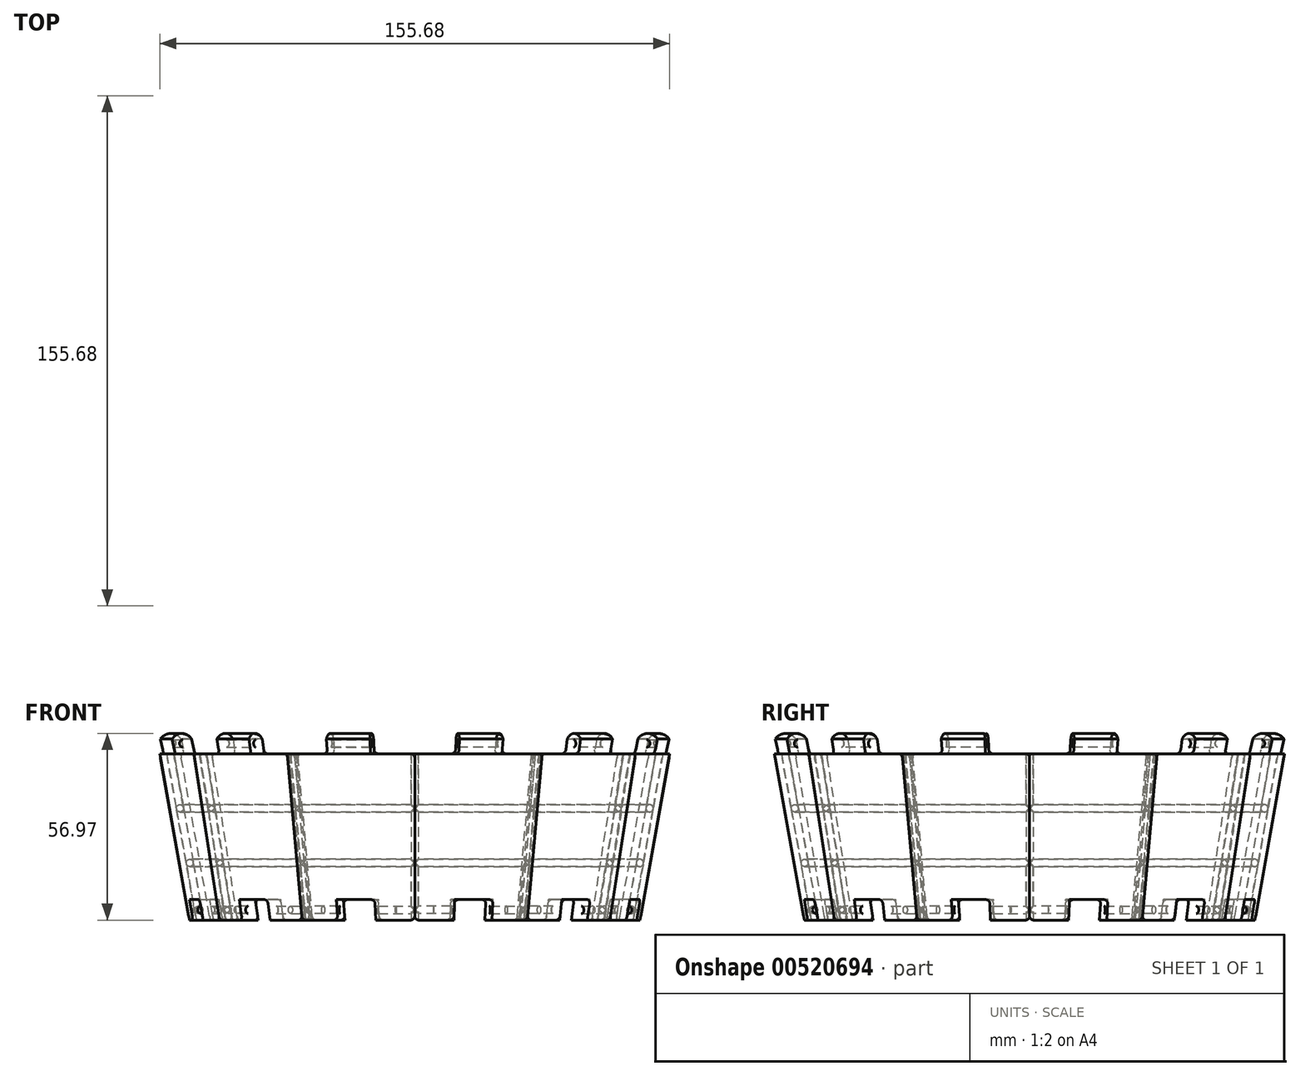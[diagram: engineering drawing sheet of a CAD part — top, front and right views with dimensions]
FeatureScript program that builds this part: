
annotation { "Feature Type Name" : "Feature", "Feature Type Description" : "" }
export const myFeature = defineFeature(function(context is Context, id is Id, definition is map)
    precondition{}
    {
        {
            var Q0;
            Q0=qCreatedBy(makeId("Front.planeOp"),FACE);
            var sketch = newSketch(context, id + "F0", { "sketchPlane" : qUnion([Q0])});
            skLineSegment(sketch, "E0", {"start": v(0, 0) * mm, "end": v(0, 50.8) * mm});
            skLineSegment(sketch, "E1", {"start": v(0, 50.8) * mm, "end": v(77.84, 50.8) * mm});
            skLineSegment(sketch, "E2", {"start": v(0, 0) * mm, "end": v(68.76, 0) * mm});
            skLineSegment(sketch, "E3", {"start": v(68.76, 0) * mm, "end": v(77.84, 50.8) * mm});
            skSolve(sketch);
        }
        {
            var Q0;
            Q0 = qSketchRegion(id + "F0", true);
            var Q1;
            Q1=sQuery(id+"F0.wireOp",EDGE,"E0");
            revolve(context, id + "F1", {"entities" : qUnion([Q0]), "axis" : qUnion([Q1]), "revolveType" : RevolveType.ONE_DIRECTION, "angle" : 30 * degree});
        }
        {
            var Q0;
            Q0=makeQuery(id+"F1.opRevolve","CAP_FACE",FACE,{"disambiguationData":[OSD([sQuery(id+"F0.wireOp",EDGE,"E0"),sQuery(id+"F0.wireOp",EDGE,"E1"),sQuery(id+"F0.wireOp",EDGE,"E2"),sQuery(id+"F0.wireOp",EDGE,"E3")])],"isStart":true});
            var sketch = newSketch(context, id + "F2", { "sketchPlane" : qUnion([Q0])});
            skLineSegment(sketch, "E4", {"start": v(0, 0) * mm, "end": v(0, 50.8) * mm});
            skLineSegment(sketch, "E5", {"start": v(0, 50.8) * mm, "end": v(71.49, 50.8) * mm});
            skLineSegment(sketch, "E6", {"start": v(0, 0) * mm, "end": v(62.4, 0) * mm});
            skLineSegment(sketch, "E7", {"start": v(62.4, 0) * mm, "end": v(71.49, 50.8) * mm});
            skSolve(sketch);
        }
        {
            var Q0;
            Q0 = qSketchRegion(id + "F2", true);
            var Q1;
            Q1=sQuery(id+"F2.wireOp",EDGE,"E4");
            revolve(context, id + "F3", {"operationType" : NewBodyOperationType.REMOVE, "entities" : qUnion([Q0]), "axis" : qUnion([Q1]), "revolveType" : RevolveType.FULL, "oppositeDirection" : true});
        }
        {
            var Q0;
            Q0=makeQuery(id+"F1.opRevolve","CAP_FACE",FACE,{"disambiguationData":[OSD([sQuery(id+"F0.wireOp",EDGE,"E0"),sQuery(id+"F0.wireOp",EDGE,"E1"),sQuery(id+"F0.wireOp",EDGE,"E2"),sQuery(id+"F0.wireOp",EDGE,"E3")])],"isStart":true});
            var sketch = newSketch(context, id + "F4", { "sketchPlane" : qUnion([Q0])});
            skLineSegment(sketch, "E8", {"start": v(0, 0) * mm, "end": v(0, 50.8) * mm, "construction": true});
            skLineSegment(sketch, "E9", {"start": v(0, 0) * mm, "end": v(68.76, 0) * mm, "construction": true});
            skLineSegment(sketch, "E10", {"start": v(68.76, 0) * mm, "end": v(69.88, 6.25) * mm});
            skLineSegment(sketch, "E11", {"start": v(69.88, 6.25) * mm, "end": v(63.53, 6.25) * mm});
            skLineSegment(sketch, "E12", {"start": v(63.53, 6.25) * mm, "end": v(62.4, 0) * mm});
            skLineSegment(sketch, "E13", {"start": v(68.76, 0) * mm, "end": v(62.4, 0) * mm});
            skSolve(sketch);
        }
        {
            var Q0;
            Q0 = qSketchRegion(id + "F4", true);
            var Q1;
            Q1=sQuery(id+"F4.wireOp",EDGE,"E8");
            revolve(context, id + "F5", {"operationType" : NewBodyOperationType.REMOVE, "entities" : qUnion([Q0]), "axis" : qUnion([Q1]), "revolveType" : RevolveType.ONE_DIRECTION, "angle" : 20 * degree});
        }
        {
            var Q0;
            Q0 = qSketchRegion(id + "F4", true);
            var Q1;
            Q1=sQuery(id+"F4.wireOp",EDGE,"E8");
            revolve(context, id + "F6", {"operationType" : NewBodyOperationType.ADD, "entities" : qUnion([Q0]), "axis" : qUnion([Q1]), "revolveType" : RevolveType.ONE_DIRECTION, "angle" : 10 * degree});
        }
        {
            var Q0;
            Q0=makeQuery(id+"F6.boolean.opBoolean","MERGE",FACE,{"derivedFrom":[makeQuery(id+"F1.opRevolve","CAP_FACE",FACE,{"disambiguationData":[OSD([sQuery(id+"F0.wireOp",EDGE,"E0"),sQuery(id+"F0.wireOp",EDGE,"E1"),sQuery(id+"F0.wireOp",EDGE,"E2"),sQuery(id+"F0.wireOp",EDGE,"E3")])],"isStart":true}),makeQuery(id+"F6.opRevolve","CAP_FACE",FACE,{"disambiguationData":[OSD([sQuery(id+"F4.wireOp",EDGE,"E10"),sQuery(id+"F4.wireOp",EDGE,"E11"),sQuery(id+"F4.wireOp",EDGE,"E12"),sQuery(id+"F4.wireOp",EDGE,"E13")])],"isStart":true})]});
            var sketch = newSketch(context, id + "F7", { "sketchPlane" : qUnion([Q0])});
            skLineSegment(sketch, "E14", {"start": v(0, 0) * mm, "end": v(0, 50.8) * mm, "construction": true});
            skLineSegment(sketch, "E15", {"start": v(77.84, 50.8) * mm, "end": v(68.76, 0) * mm, "construction": true});
            skLineSegment(sketch, "E16", {"start": v(77.84, 50.8) * mm, "end": v(71.49, 50.8) * mm});
            skLineSegment(sketch, "E17", {"start": v(0, 50.8) * mm, "end": v(0, 101.6) * mm, "construction": true});
            skLineSegment(sketch, "E18", {"start": v(0, 101.6) * mm, "end": v(88.9, 101.6) * mm, "construction": true});
            skLineSegment(sketch, "E19", {"start": v(88.9, 101.6) * mm, "end": v(77.84, 50.8) * mm, "construction": true});
            skLineSegment(sketch, "E20", {"start": v(77.84, 50.8) * mm, "end": v(79.19, 57) * mm});
            skLineSegment(sketch, "E21", {"start": v(79.19, 57) * mm, "end": v(72.84, 57) * mm});
            skLineSegment(sketch, "E22", {"start": v(72.84, 57) * mm, "end": v(71.49, 50.8) * mm});
            skSolve(sketch);
        }
        {
            var Q0;
            Q0 = qSketchRegion(id + "F7", true);
            var Q1;
            Q1=sQuery(id+"F7.wireOp",EDGE,"E14");
            revolve(context, id + "F8", {"operationType" : NewBodyOperationType.ADD, "entities" : qUnion([Q0]), "axis" : qUnion([Q1]), "revolveType" : RevolveType.ONE_DIRECTION, "angle" : 20 * degree});
        }
        {
            var Q0;
            Q0 = qSketchRegion(id + "F7", true);
            var Q1;
            Q1=sQuery(id+"F7.wireOp",EDGE,"E14");
            revolve(context, id + "F9", {"operationType" : NewBodyOperationType.REMOVE, "entities" : qUnion([Q0]), "axis" : qUnion([Q1]), "revolveType" : RevolveType.ONE_DIRECTION, "angle" : 10 * degree});
        }
        {
            var Q0;
            Q0=makeQuery(id+"F5.boolean.opBoolean","COPY",EDGE,{"derivedFrom":makeQuery(id+"F5.opRevolve","CAP_EDGE",EDGE,{"disambiguationData":[OSD([sQuery(id+"F4.wireOp",EDGE,"E11")])],"isStart":false})});
            var Q1;
            Q1=makeQuery(id+"F6.opRevolve","CAP_EDGE",EDGE,{"disambiguationData":[OSD([sQuery(id+"F4.wireOp",EDGE,"E11")])],"isStart":false});
            var Q2;
            Q2=makeQuery(id+"F6.opRevolve","CAP_EDGE",EDGE,{"disambiguationData":[OSD([sQuery(id+"F4.wireOp",EDGE,"E13")])],"isStart":false});
            var Q3;
            Q3=makeQuery(id+"F5.boolean.opBoolean","COPY",EDGE,{"derivedFrom":makeQuery(id+"F5.opRevolve","CAP_EDGE",EDGE,{"disambiguationData":[OSD([sQuery(id+"F4.wireOp",EDGE,"E13")])],"isStart":false})});
            var Q4;
            Q4=makeQuery(id+"F6.opRevolve","CAP_EDGE",EDGE,{"disambiguationData":[OSD([sQuery(id+"F4.wireOp",EDGE,"E13")])],"isStart":true});
            var Q5;
            Q5=makeQuery(id+"F1.opRevolve","CAP_EDGE",EDGE,{"disambiguationData":[OSD([sQuery(id+"F0.wireOp",EDGE,"E2")])],"isStart":false});
            var Q6;
            Q6=makeQuery(id+"F8.opRevolve","CAP_EDGE",EDGE,{"disambiguationData":[OSD([sQuery(id+"F7.wireOp",EDGE,"E16")])],"isStart":false});
            var Q7;
            Q7=makeQuery(id+"F1.opRevolve","CAP_EDGE",EDGE,{"disambiguationData":[OSD([sQuery(id+"F0.wireOp",EDGE,"E1")])],"isStart":false});
            var Q8;
            Q8=makeQuery(id+"F8.opRevolve","CAP_EDGE",EDGE,{"disambiguationData":[OSD([sQuery(id+"F7.wireOp",EDGE,"E21")])],"isStart":false});
            var Q9;
            Q9=makeQuery(id+"F9.boolean.opBoolean","COPY",EDGE,{"derivedFrom":makeQuery(id+"F9.opRevolve","CAP_EDGE",EDGE,{"disambiguationData":[OSD([sQuery(id+"F7.wireOp",EDGE,"E21")])],"isStart":false})});
            var Q10;
            Q10=makeQuery(id+"F9.boolean.opBoolean","COPY",EDGE,{"derivedFrom":makeQuery(id+"F9.opRevolve","CAP_EDGE",EDGE,{"disambiguationData":[OSD([sQuery(id+"F7.wireOp",EDGE,"E16")])],"isStart":false})});
            var Q11;
            Q11=makeQuery(id+"F9.boolean.opBoolean","COPY",EDGE,{"derivedFrom":makeQuery(id+"F9.opRevolve","CAP_EDGE",EDGE,{"disambiguationData":[OSD([sQuery(id+"F7.wireOp",EDGE,"E16")])],"isStart":true})});
            fillet(context, id + "F10", {"entities" : qUnion([Q0, Q1, Q2, Q3, Q4, Q5, Q6, Q7, Q8, Q9, Q10, Q11]), "radius" : 1.27 * mm, "tangentPropagation" : true, "allowEdgeOverflow" : false});
        }
        {
            var Q0;
            Q0=makeQuery(id+"F8.boolean.opBoolean","MERGE",FACE,{"derivedFrom":[makeQuery(id+"F6.boolean.opBoolean","MERGE",FACE,{"derivedFrom":[makeQuery(id+"F1.opRevolve","CAP_FACE",FACE,{"disambiguationData":[OSD([sQuery(id+"F0.wireOp",EDGE,"E0"),sQuery(id+"F0.wireOp",EDGE,"E1"),sQuery(id+"F0.wireOp",EDGE,"E2"),sQuery(id+"F0.wireOp",EDGE,"E3")])],"isStart":true}),makeQuery(id+"F6.opRevolve","CAP_FACE",FACE,{"disambiguationData":[OSD([sQuery(id+"F4.wireOp",EDGE,"E10"),sQuery(id+"F4.wireOp",EDGE,"E11"),sQuery(id+"F4.wireOp",EDGE,"E12"),sQuery(id+"F4.wireOp",EDGE,"E13")])],"isStart":true})]}),makeQuery(id+"F8.opRevolve","CAP_FACE",FACE,{"disambiguationData":[OSD([sQuery(id+"F7.wireOp",EDGE,"E16"),sQuery(id+"F7.wireOp",EDGE,"E20"),sQuery(id+"F7.wireOp",EDGE,"E21"),sQuery(id+"F7.wireOp",EDGE,"E22")])],"isStart":true})]});
            var sketch = newSketch(context, id + "F11", { "sketchPlane" : qUnion([Q0])});
            skLineSegment(sketch, "E23", {"start": v(0, 0) * mm, "end": v(0, 50.8) * mm, "construction": true});
            skLineSegment(sketch, "E24", {"start": v(0, 50.8) * mm, "end": v(77.84, 50.8) * mm, "construction": true});
            skLineSegment(sketch, "E25", {"start": v(0, 0) * mm, "end": v(68.76, 0) * mm, "construction": true});
            skLineSegment(sketch, "E26", {"start": v(68.76, 0) * mm, "end": v(77.84, 50.8) * mm, "construction": true});
            skLineSegment(sketch, "E27", {"start": v(77.84, 50.8) * mm, "end": v(76.72, 44.55) * mm, "construction": true});
            skLineSegment(sketch, "E28", {"start": v(68.76, 0) * mm, "end": v(69.32, 3.13) * mm, "construction": true});
            skCircle(sketch, "E29", {"center": v(66.14, 3.13) * mm, "radius": 1.11 * mm});
            skLineSegment(sketch, "E30", {"start": v(77.84, 50.8) * mm, "end": v(78.4, 53.93) * mm, "construction": true});
            skLineSegment(sketch, "E31", {"start": v(78.4, 53.93) * mm, "end": v(75.22, 53.93) * mm, "construction": true});
            skCircle(sketch, "E32", {"center": v(75.22, 53.93) * mm, "radius": 1.11 * mm});
            skLineSegment(sketch, "E33", {"start": v(68.76, 0) * mm, "end": v(65.58, 0) * mm, "construction": true});
            skLineSegment(sketch, "E34", {"start": v(65.58, 0) * mm, "end": v(74.66, 50.8) * mm, "construction": true});
            skLineSegment(sketch, "E35", {"start": v(74.66, 50.8) * mm, "end": v(71.68, 34.13) * mm, "construction": true});
            skLineSegment(sketch, "E36", {"start": v(71.68, 34.13) * mm, "end": v(68.7, 17.46) * mm, "construction": true});
            skCircle(sketch, "E37", {"center": v(71.68, 34.13) * mm, "radius": 1.11 * mm});
            skCircle(sketch, "E38", {"center": v(68.7, 17.46) * mm, "radius": 1.11 * mm});
            skSolve(sketch);
        }
        {
            var Q0;
            Q0 = qSketchRegion(id + "F11", true);
            var Q1;
            Q1=sQuery(id+"F11.wireOp",EDGE,"E23");
            revolve(context, id + "F12", {"operationType" : NewBodyOperationType.REMOVE, "entities" : qUnion([Q0]), "axis" : qUnion([Q1]), "revolveType" : RevolveType.FULL, "oppositeDirection" : true});
        }
        {
            var Q0;
            Q0=makeQuery(id+"F11.imprint","IMPRINT",FACE,{"disambiguationData":[TD([[makeQuery(id+"F11.imprint","IMPRINT",EDGE,{"derivedFrom":sQuery(id+"F11.wireOp",EDGE,"E29")}),1.0]])]});
            var Q1;
            Q1=sQuery(id+"F11.wireOp",EDGE,"E23");
            revolve(context, id + "F13", {"operationType" : NewBodyOperationType.ADD, "entities" : qUnion([Q0]), "axis" : qUnion([Q1]), "revolveType" : RevolveType.ONE_DIRECTION, "angle" : 5 * degree});
        }
        {
            var Q0;
            Q0=makeQuery(id+"F12.boolean.opBoolean","INTERSECT",EDGE,{"derivedFrom":[makeQuery(id+"F8.boolean.opBoolean","MERGE",FACE,{"derivedFrom":[makeQuery(id+"F6.boolean.opBoolean","MERGE",FACE,{"derivedFrom":[makeQuery(id+"F1.opRevolve","CAP_FACE",FACE,{"disambiguationData":[OSD([sQuery(id+"F0.wireOp",EDGE,"E0"),sQuery(id+"F0.wireOp",EDGE,"E1"),sQuery(id+"F0.wireOp",EDGE,"E2"),sQuery(id+"F0.wireOp",EDGE,"E3")])],"isStart":true}),makeQuery(id+"F6.opRevolve","CAP_FACE",FACE,{"disambiguationData":[OSD([sQuery(id+"F4.wireOp",EDGE,"E10"),sQuery(id+"F4.wireOp",EDGE,"E11"),sQuery(id+"F4.wireOp",EDGE,"E12"),sQuery(id+"F4.wireOp",EDGE,"E13")])],"isStart":true})]}),makeQuery(id+"F8.opRevolve","CAP_FACE",FACE,{"disambiguationData":[OSD([sQuery(id+"F7.wireOp",EDGE,"E16"),sQuery(id+"F7.wireOp",EDGE,"E20"),sQuery(id+"F7.wireOp",EDGE,"E21"),sQuery(id+"F7.wireOp",EDGE,"E22")])],"isStart":true})]}),makeQuery(id+"F12.opRevolve","SWEPT_FACE",FACE,{"disambiguationData":[OSD([sQuery(id+"F11.wireOp",EDGE,"aBI1GnQK-pT2i-Mksw-Z7v4-IHPqoVV2bVJO")])]})]});
            var Q1;
            Q1=makeQuery(id+"F12.boolean.opBoolean","INTERSECT",EDGE,{"derivedFrom":[makeQuery(id+"F8.boolean.opBoolean","MERGE",FACE,{"derivedFrom":[makeQuery(id+"F6.boolean.opBoolean","MERGE",FACE,{"derivedFrom":[makeQuery(id+"F1.opRevolve","CAP_FACE",FACE,{"disambiguationData":[OSD([sQuery(id+"F0.wireOp",EDGE,"E0"),sQuery(id+"F0.wireOp",EDGE,"E1"),sQuery(id+"F0.wireOp",EDGE,"E2"),sQuery(id+"F0.wireOp",EDGE,"E3")])],"isStart":true}),makeQuery(id+"F6.opRevolve","CAP_FACE",FACE,{"disambiguationData":[OSD([sQuery(id+"F4.wireOp",EDGE,"E10"),sQuery(id+"F4.wireOp",EDGE,"E11"),sQuery(id+"F4.wireOp",EDGE,"E12"),sQuery(id+"F4.wireOp",EDGE,"E13")])],"isStart":true})]}),makeQuery(id+"F8.opRevolve","CAP_FACE",FACE,{"disambiguationData":[OSD([sQuery(id+"F7.wireOp",EDGE,"E16"),sQuery(id+"F7.wireOp",EDGE,"E20"),sQuery(id+"F7.wireOp",EDGE,"E21"),sQuery(id+"F7.wireOp",EDGE,"E22")])],"isStart":true})]}),makeQuery(id+"F12.opRevolve","SWEPT_FACE",FACE,{"disambiguationData":[OSD([sQuery(id+"F11.wireOp",EDGE,"E29")])]})]});
            var Q2;
            Q2=makeQuery(id+"F12.boolean.opBoolean","INTERSECT",EDGE,{"derivedFrom":[makeQuery(id+"F1.opRevolve","CAP_FACE",FACE,{"disambiguationData":[OSD([sQuery(id+"F0.wireOp",EDGE,"E0"),sQuery(id+"F0.wireOp",EDGE,"E1"),sQuery(id+"F0.wireOp",EDGE,"E2"),sQuery(id+"F0.wireOp",EDGE,"E3")])],"isStart":false}),makeQuery(id+"F12.opRevolve","SWEPT_FACE",FACE,{"disambiguationData":[OSD([sQuery(id+"F11.wireOp",EDGE,"E29")])]})]});
            var Q3;
            Q3=makeQuery(id+"F12.boolean.opBoolean","INTERSECT",EDGE,{"derivedFrom":[makeQuery(id+"F1.opRevolve","CAP_FACE",FACE,{"disambiguationData":[OSD([sQuery(id+"F0.wireOp",EDGE,"E0"),sQuery(id+"F0.wireOp",EDGE,"E1"),sQuery(id+"F0.wireOp",EDGE,"E2"),sQuery(id+"F0.wireOp",EDGE,"E3")])],"isStart":false}),makeQuery(id+"F12.opRevolve","SWEPT_FACE",FACE,{"disambiguationData":[OSD([sQuery(id+"F11.wireOp",EDGE,"aBI1GnQK-pT2i-Mksw-Z7v4-IHPqoVV2bVJO")])]})]});
            var Q4;
            Q4=makeQuery(id+"F12.boolean.opBoolean","INTERSECT",EDGE,{"derivedFrom":[makeQuery(id+"F9.boolean.opBoolean","COPY",FACE,{"derivedFrom":makeQuery(id+"F9.opRevolve","CAP_FACE",FACE,{"disambiguationData":[OSD([sQuery(id+"F7.wireOp",EDGE,"E16"),sQuery(id+"F7.wireOp",EDGE,"E20"),sQuery(id+"F7.wireOp",EDGE,"E21"),sQuery(id+"F7.wireOp",EDGE,"E22")])],"isStart":false})}),makeQuery(id+"F12.opRevolve","SWEPT_FACE",FACE,{"disambiguationData":[OSD([sQuery(id+"F11.wireOp",EDGE,"E32")])]})]});
            var Q5;
            Q5=makeQuery(id+"F12.boolean.opBoolean","INTERSECT",EDGE,{"derivedFrom":[makeQuery(id+"F8.opRevolve","CAP_FACE",FACE,{"disambiguationData":[OSD([sQuery(id+"F7.wireOp",EDGE,"E16"),sQuery(id+"F7.wireOp",EDGE,"E20"),sQuery(id+"F7.wireOp",EDGE,"E21"),sQuery(id+"F7.wireOp",EDGE,"E22")])],"isStart":false}),makeQuery(id+"F12.opRevolve","SWEPT_FACE",FACE,{"disambiguationData":[OSD([sQuery(id+"F11.wireOp",EDGE,"E32")])]})]});
            var Q6;
            Q6=makeQuery(id+"F12.boolean.opBoolean","INTERSECT",EDGE,{"derivedFrom":[makeQuery(id+"F6.opRevolve","CAP_FACE",FACE,{"disambiguationData":[OSD([sQuery(id+"F4.wireOp",EDGE,"E10"),sQuery(id+"F4.wireOp",EDGE,"E11"),sQuery(id+"F4.wireOp",EDGE,"E12"),sQuery(id+"F4.wireOp",EDGE,"E13")])],"isStart":false}),makeQuery(id+"F12.opRevolve","SWEPT_FACE",FACE,{"disambiguationData":[OSD([sQuery(id+"F11.wireOp",EDGE,"E29")])]})]});
            var Q7;
            Q7=makeQuery(id+"F12.boolean.opBoolean","INTERSECT",EDGE,{"derivedFrom":[makeQuery(id+"F5.boolean.opBoolean","COPY",FACE,{"derivedFrom":makeQuery(id+"F5.opRevolve","CAP_FACE",FACE,{"disambiguationData":[OSD([sQuery(id+"F4.wireOp",EDGE,"E10"),sQuery(id+"F4.wireOp",EDGE,"E11"),sQuery(id+"F4.wireOp",EDGE,"E12"),sQuery(id+"F4.wireOp",EDGE,"E13")])],"isStart":false})}),makeQuery(id+"F12.opRevolve","SWEPT_FACE",FACE,{"disambiguationData":[OSD([sQuery(id+"F11.wireOp",EDGE,"E29")])]})]});
            fillet(context, id + "F14", {"entities" : qUnion([Q0, Q1, Q2, Q3, Q4, Q5, Q6, Q7]), "radius" : 0.32 * mm, "tangentPropagation" : true, "allowEdgeOverflow" : false});
        }
        {
            var Q0;
            Q0=qCreatedBy(makeId("Front.planeOp"),FACE);
            var sketch = newSketch(context, id + "F15", { "sketchPlane" : qUnion([Q0])});
            skLineSegment(sketch, "E39", {"start": v(0, 0) * mm, "end": v(0, 38.2) * mm, "construction": true});
            skSolve(sketch);
        }
        {
            var Q0;
            Q0=makeQuery(id+"F6.opRevolve","SWEPT_FACE",FACE,{"disambiguationData":[OSD([sQuery(id+"F4.wireOp",EDGE,"E13")])]});
            var sketch = newSketch(context, id + "F16", { "sketchPlane" : qUnion([Q0])});
            skLineSegment(sketch, "E40", {"start": v(0, 0) * mm, "end": v(68.75, 0) * mm, "construction": true});
            skPoint(sketch, "E41", {"position": v(65.57, 0) * mm});
            skCircle(sketch, "E42", {"center": v(65.57, 0) * mm, "radius": 1.11 * mm});
            skLineSegment(sketch, "E43", {"start": v(0, 0) * mm, "end": v(59.54, -34.37) * mm, "construction": true});
            skPoint(sketch, "E44", {"position": v(56.79, -32.79) * mm});
            skCircle(sketch, "E45", {"center": v(56.79, -32.79) * mm, "radius": 1.11 * mm});
            skSolve(sketch);
        }
        {
            var Q0;
            Q0=makeQuery(id+"F9.boolean.opBoolean","COPY",FACE,{"derivedFrom":makeQuery(id+"F9.opRevolve","SWEPT_FACE",FACE,{"disambiguationData":[OSD([sQuery(id+"F7.wireOp",EDGE,"E16")])]})});
            var sketch = newSketch(context, id + "F17", { "sketchPlane" : qUnion([Q0])});
            skLineSegment(sketch, "E46", {"start": v(0, 0) * mm, "end": v(77.83, 0) * mm, "construction": true});
            skLineSegment(sketch, "E47", {"start": v(77.83, 0) * mm, "end": v(74.65, 0) * mm, "construction": true});
            skCircle(sketch, "E48", {"center": v(74.65, 0) * mm, "radius": 1.11 * mm});
            skLineSegment(sketch, "E49", {"start": v(0, 0) * mm, "end": v(67.4, 38.91) * mm, "construction": true});
            skPoint(sketch, "E50", {"position": v(64.65, 37.33) * mm});
            skCircle(sketch, "E51", {"center": v(64.65, 37.33) * mm, "radius": 1.11 * mm});
            skSolve(sketch);
        }
        {
            var Q1;
            Q1=makeQuery(id+"F17.imprint","IMPRINT",FACE,{"disambiguationData":[TD([[makeQuery(id+"F17.imprint","IMPRINT",EDGE,{"derivedFrom":sQuery(id+"F17.wireOp",EDGE,"E48")}),1.0]])]});
            var Q2;
            Q2=makeQuery(id+"F16.imprint","IMPRINT",FACE,{"disambiguationData":[TD([[makeQuery(id+"F16.imprint","IMPRINT",EDGE,{"derivedFrom":sQuery(id+"F16.wireOp",EDGE,"E42")}),1.0]])]});
            loft(context, id + "F18", {"operationType" : NewBodyOperationType.REMOVE, "sheetProfilesArray" : [{ "sheetProfileEntities" : qUnion([Q1]) }, { "sheetProfileEntities" : qUnion([Q2]) }]});
        }
        {
            var Q1;
            Q1=makeQuery(id+"F17.imprint","IMPRINT",FACE,{"disambiguationData":[TD([[makeQuery(id+"F17.imprint","IMPRINT",EDGE,{"derivedFrom":sQuery(id+"F17.wireOp",EDGE,"E51")}),1.0]])]});
            var Q2;
            Q2=makeQuery(id+"F16.imprint","IMPRINT",FACE,{"disambiguationData":[TD([[makeQuery(id+"F16.imprint","IMPRINT",EDGE,{"derivedFrom":sQuery(id+"F16.wireOp",EDGE,"E45")}),1.0]])]});
            loft(context, id + "F19", {"operationType" : NewBodyOperationType.REMOVE, "sheetProfilesArray" : [{ "sheetProfileEntities" : qUnion([Q1]) }, { "sheetProfileEntities" : qUnion([Q2]) }]});
        }
        {
            var Q0;
            Q0=qCreatedBy(makeId("Front.planeOp"),FACE);
            var sketch = newSketch(context, id + "F20", { "sketchPlane" : qUnion([Q0])});
            skLineSegment(sketch, "E52", {"start": v(0, 0) * mm, "end": v(68.76, 0) * mm, "construction": true});
            skLineSegment(sketch, "E53", {"start": v(0, 0) * mm, "end": v(0, 50.8) * mm, "construction": true});
            skLineSegment(sketch, "E54", {"start": v(0, 50.8) * mm, "end": v(74.5, 50.8) * mm, "construction": true});
            skLineSegment(sketch, "E55", {"start": v(77.85, 50.8) * mm, "end": v(68.76, 0) * mm, "construction": true});
            skLineSegment(sketch, "E56", {"start": v(0, 50.8) * mm, "end": v(0, 101.6) * mm, "construction": true});
            skLineSegment(sketch, "E57", {"start": v(0, 101.6) * mm, "end": v(88.9, 101.6) * mm, "construction": true});
            skLineSegment(sketch, "E58", {"start": v(88.9, 101.6) * mm, "end": v(77.85, 50.8) * mm, "construction": true});
            skLineSegment(sketch, "E59", {"start": v(77.85, 50.8) * mm, "end": v(71.5, 50.8) * mm, "construction": true});
            skLineSegment(sketch, "E60", {"start": v(77.85, 50.8) * mm, "end": v(78.82, 55.27) * mm, "construction": true});
            skLineSegment(sketch, "E61", {"start": v(72.47, 55.27) * mm, "end": v(71.5, 50.8) * mm, "construction": true});
            skLineSegment(sketch, "E62", {"start": v(78.82, 55.27) * mm, "end": v(79.57, 58.72) * mm});
            skLineSegment(sketch, "E63", {"start": v(79.57, 58.72) * mm, "end": v(72.84, 58.72) * mm});
            skArc(sketch, "E64", {"start": v(78.82, 55.27) * mm, "mid": v(75.65, 56.97) * mm, "end": v(72.47, 55.27) * mm});
            skLineSegment(sketch, "E65", {"start": v(72.47, 55.27) * mm, "end": v(72.13, 55.27) * mm});
            skLineSegment(sketch, "E66", {"start": v(72.13, 55.27) * mm, "end": v(72.84, 58.72) * mm});
            skSolve(sketch);
        }
        {
            var Q0;
            Q0 = qSketchRegion(id + "F20", true);
            var Q1;
            Q1=sQuery(id+"F20.wireOp",EDGE,"E53");
            revolve(context, id + "F21", {"operationType" : NewBodyOperationType.REMOVE, "entities" : qUnion([Q0]), "axis" : qUnion([Q1]), "revolveType" : RevolveType.FULL, "oppositeDirection" : true});
        }
        {
            var Q0;
            Q0=makeQuery(id+"F1.opRevolve","SWEPT_BODY",BODY,{"disambiguationData":[OSD([sQuery(id+"F0.wireOp",EDGE,"E0"),sQuery(id+"F0.wireOp",EDGE,"E1"),sQuery(id+"F0.wireOp",EDGE,"E2"),sQuery(id+"F0.wireOp",EDGE,"E3")])]});
            var Q1;
            Q1=sQuery(id+"F15.wireOp",EDGE,"E39");
            circularPattern(context, id + "F22", {"entities" : qUnion([Q0]), "axis" : qUnion([Q1]), "angle" : 360 * degree, "instanceCount" : 12, "equalSpace" : true});
        }
    });
